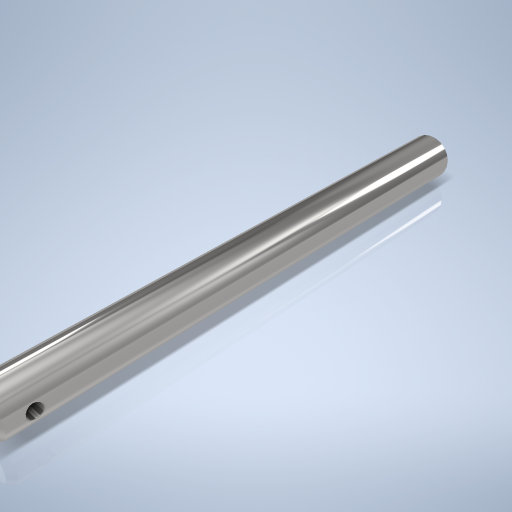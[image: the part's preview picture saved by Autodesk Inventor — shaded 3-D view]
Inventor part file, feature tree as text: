
AUTODESK INVENTOR PART (.ipt)
format: ipt  version: 2024.2 (Build 282272000, 272)  size: 289,792 bytes
history: native  units: mm
features: sketch x2, extrude x1, chamfer x1, plane x1, hole x1
ambient origin geometry x8: Origin, YZ Plane, XZ Plane, XY Plane, X Axis, Y Axis, Z Axis, Center Point
bodies: Volumenkörper1 (feature_tree)
feature tree (6):
  extrude  "Extrusion1"  Depth=73.0mm TaperAngle=0.0deg
  chamfer  "Fasen1"  Distance=0.8mm Angle=45.0deg
  plane  "Arbeitsebene1"
  hole  "Bohrung1"  [1 undecoded]
  sketch  "Skizze1"  dims[d0=6.5mm d1=73.0mm d2=0.0mm d3=0.8mm d4=2.0mm d5=45.0deg]
  sketch  "Skizze2"  dims[d6=3.25mm d7=4.0mm d8=2.0mm d9=6.0mm d10=4.0mm d11=2.0mm d12=90.0deg d13=8.0mm d14=0.0mm d15=0.5mm d16=0.872665mm d17=0.5mm d18=0.872665mm]
note: 1 required parameter value undecoded (feature->parameter linkage not recoverable at this tier; creation-order binding heuristic only, values carry confidence <= 0.55)
